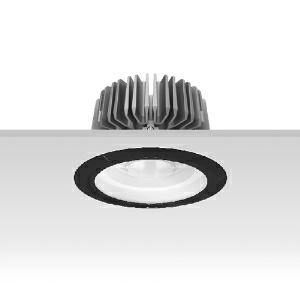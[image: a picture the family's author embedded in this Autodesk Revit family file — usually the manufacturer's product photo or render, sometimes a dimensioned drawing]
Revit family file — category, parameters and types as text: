
# Revit family: 3f_filippi_-_3f_reno_bianco_ampio_3f_filippi_-_30383_a01024_-_3f_reno_150_wh_3000-840_dali_wide___vt_bk_1bad
name_source: partatom
category: Lighting Fixtures
units: mm (PartAtom-declared; Revit-internal decimal feet)

## family parameters
Cut with Voids When Loaded = No
Host = Face
Light Source = No
Part Type = Normal
Room Calculation Point = No
Round Connector Dimension = Use Diameter
Shared = No

## types (1)
- 3F Filippi - 3F Reno Bianco Ampio (1 x LED, 2647 lm, 28 W, 4000 K)
    Apparent Load = 28 VA
    Approval mark = CE
    CIE Flux Codes = 74 93 99 100 100
    Color Rendering = 80
    Color Temperature = 4000 K
    Control Gear = Electronic transformer
    Default Elevation = 1800 mm
    Description = ILLUMINOTECHNICAL
Luminous efficiency 100% (DLOR 100%, ULOR 0%).
Initial luminous flux of the luminaire 2647 lm.
Direct symmetric wide distribution.
Installation Interdistance Transv.D = 1.54 x hu - Long.D = 1.54 x hu.
Tabular UGR (CIE 117 - 4H-8H; S=0.25H; 70/50/20): RUG 24.4 - 24.2.
Beam angle: 74° - 73°.
Luminous efficacy 95 lm/W.
Lifetime (L90/B10): 30000 h. (tq+25°C)
Lifetime (L85/B10): 50000 h. (tq+25°C)
Lifetime (L70/B10): 80000 h. (tq+25°C)
Sudden decreased luminous flux after 50000 hours: 0% (C0).
Photobiological safety in compliance with IEC/TR 62778: RG0 risk exempt, (IEC 62471).
In compliance with IEC/EN 62722-2-1 - IEC/EN 62717 standards.

SOURCE
Compact LED module 3000/840.
Energy efficiency class (UE 2019/2020 - UE 2019/2015): E.
CIE 13.3 Colour rendering index: CRI >80 (R9 <50%).
IES TM-30 Fidelity Index: Rf = 84 Rg = 95.
CCT nominal colour temperature 4000 K.
Colour initial tolerance (MacAdam): SDCM 3.
Zhaga Book 3 compliant.

MECHANICAL
Passive heat dissipator in die-casting aluminium, oversized, for optimum thermal management of the LED module.
Parabolic element with graduated/concentric rings in white polycarbonate.
Transparent external lens with glossy and satin differentiated surfaces, with a cooling and anti-insect system in methacrylate (PMMA).
Fastening spring clips in stainless steel.
Dimensions: diameter 176 mm, height 111 mm. Weight 1.4 kg.
IP44 protection degree for exposed part, IP20 for recessed part.
Mechanical strength to impacts IK06 (1 joule).
Glow-wire test resistance 650°C.

ELECTRICAL
Wiring on a separate unit.
Halogen Free DALI-2 DATI (Parts 251, 252, 253), PUSH-DIM, electronic wiring 230V-50/60Hz, power factor 0.97 at full load, THD <25%, constant output current, SELV, class II, 1 driver, 1 DALI addresse.
Power of the luminaire 28 W.
ENEC - CE.
SAFE FLICKER: PstLM=<1 and SVM=<0.4 (IEC TR 61547-1 and IEC TR 63158), to ensure a more comfortable and safe light.
Luminaire compliant with EN 60598-2-22 for power supply from a centralised emergency system CPSS (Central Power Supply System), not incorporated in the luminaire - high risk areas excluded. The default power and flux are 100% in AC and 100% in DC.
Ambient temperature from 0°C to +25°C.
Temperature class T6 max 85°C.
Relative humidity UR: <85%.

INSTALLATION
Pull-up recessed fitting.
False ceiling carving: 150 mm.
All accessories dedicated to this product are available on the Catalog and on our website www.3F-Filippi.com.

ACCESSORIES
A01024 - VT transparent glass, tempered, not flammable, locked and in line with the trim, in black polycarbonate.

APPLICATIONS
Environments: architectural, commercial, exhibition areas, transit areas, corridors, shops, display windows, service areas.
In false ceilings with narrow voids.

LIGHT MANAGEMENT
Recommended minimum setting: 10%.
The luminaire, equipped with (DALI-2 DATI) driver, can be controlled manually with 3F Easy Dim technology or automatically/manually with wired or wireless DALI/D2D control systems.
The D2D driver guarantees interoperability with other devices with the same certification by making the following information available:
Device Data (Part 251), Energy Report (Part 252), Diagnosis & Maintenance (Part 253).
In electrical systems without a regulation system (manual or automatic) and DALI bus, a suitable jumper must be made on the DA-DA terminals of the appliance.

WARNING
Luminaire designed for disposal/recycling at end-of-life.
Replaceable (LED only) light source by a professional. Replaceable control gear by a professional.
    Height = 0 mm  [stored 0 ft]
    Lamp = 1 x LED
    Lamp Light Flux = 2647 lm
    Lamp Power = 28 W
    Lamp count = 1
    Length = 176 mm
    Lifetime = 50000 h
    Luminous efficacy = 95 lm/W
    Manufacturer = 3F Filippi
    ModVariant = No
    Model = 3F Filippi - 30383+A01024 - 3F Reno 150 WH 3000-840 DALI WIDE + VT BK
    Mounting Place = Ceiling
    Mounting Type = Recessed
    Number of Poles = 1
    OnlyDefault = Yes
    Power Factor = 1
    Product Name = 3F Filippi - 3F Reno Bianco Ampio
    Product group = recessed luminaire
    ProductGroupID = 4
    Protection Class = Protection class II
    Protection Degree = IP 20
    RLX_Detail_Level = 1
    RLX_Emergency_Light_Flux = 0 lm
    RLX_Emergency_Type = 0
    RLX_Emergency_Type_DB = No
    RlxData = <blob elided: 91005 chars, md5=42bdfd38>
    Socket = socket
    Standby Power = 0 W
    System Light Flux = 2647 lm
    System Power = 28 W
    Type Comments = Product without accessories
    Type Image = 3ffilippi_3f_reno_150_wh_d150__a01024.jpg
    URL = http://relux.com
    VarID = ---
    Voltage = 0 V
    Weight = 0.00 kg
    Width = 0 mm  [stored 0 ft]

note: [stored X ft] marks values corroborated as IEEE doubles in the binary element streams (Revit-internal decimal feet)

## geometry (parser evidence)
native form markers: Blend x4, Sweep x12
no freeform markers — native parametric forms only
